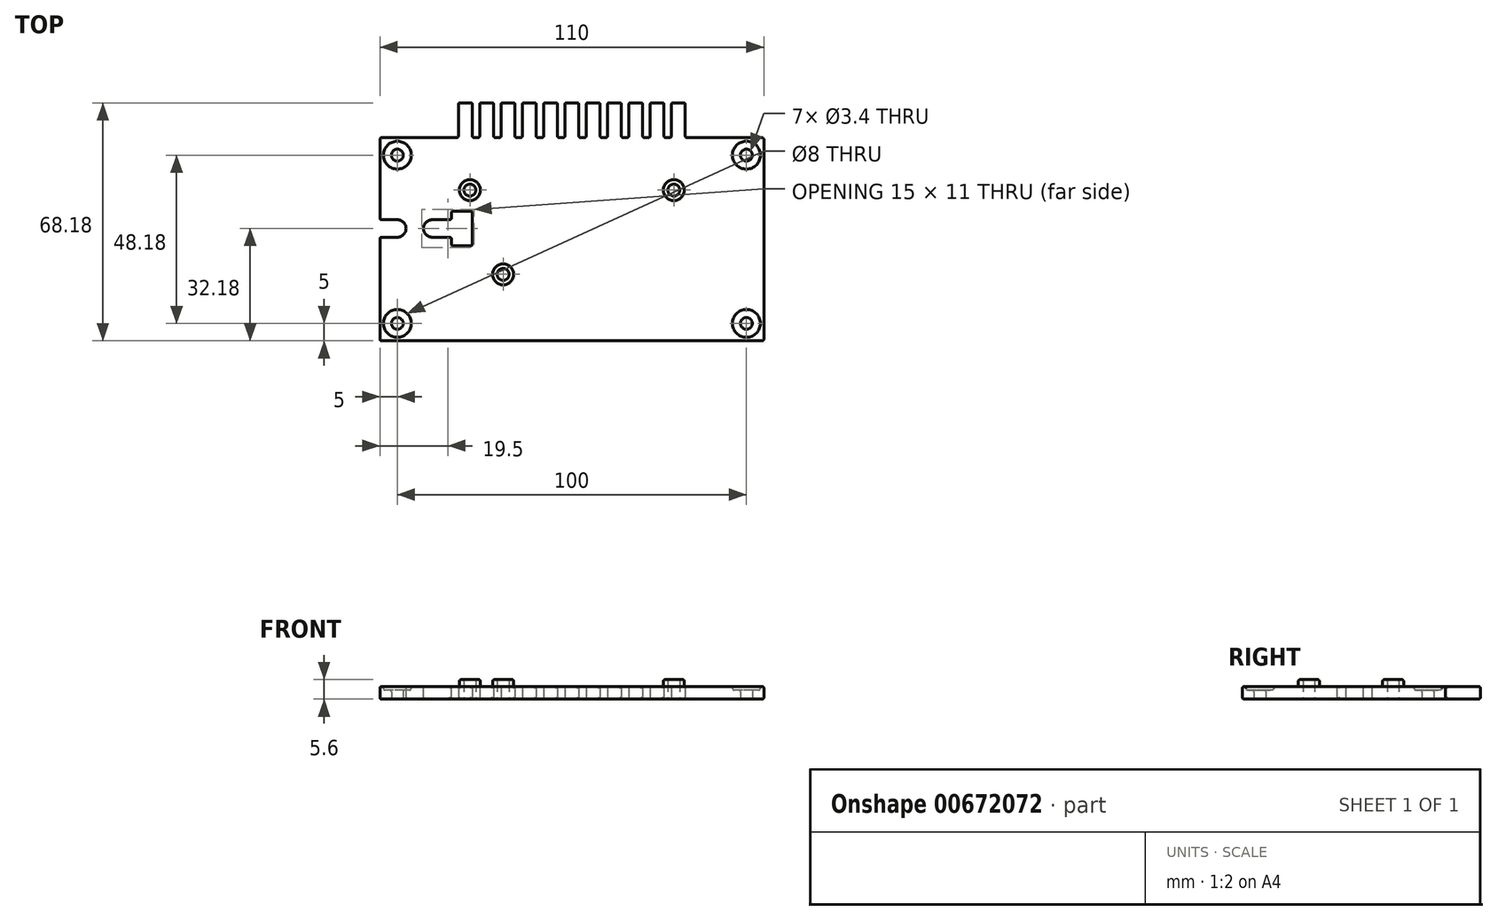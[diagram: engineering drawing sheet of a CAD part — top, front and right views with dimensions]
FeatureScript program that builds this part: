
annotation { "Feature Type Name" : "Feature", "Feature Type Description" : "" }
export const myFeature = defineFeature(function(context is Context, id is Id, definition is map)
    precondition{}
    {
        {
            var Q0;
            Q0=qCreatedBy(makeId("Top.planeOp"),FACE);
            var sketch = newSketch(context, id + "F0", { "sketchPlane" : qUnion([Q0])});
            skLineSegment(sketch, "E0.bottom", {"start": v(31.75, 16.63) * mm, "end": v(-31.75, 16.63) * mm, "construction": true});
            skLineSegment(sketch, "E0.top", {"start": v(31.75, -29.09) * mm, "end": v(-31.75, -29.09) * mm});
            skLineSegment(sketch, "E0.left", {"start": v(31.75, 16.63) * mm, "end": v(31.75, -29.1) * mm, "construction": true});
            skLineSegment(sketch, "E0.right", {"start": v(-31.75, 16.63) * mm, "end": v(-31.75, -29.1) * mm, "construction": true});
            skCircle(sketch, "E1", {"center": v(-29.21, 14.1) * mm, "radius": 1.7 * mm});
            skCircle(sketch, "E2", {"center": v(29.21, 14.1) * mm, "radius": 1.7 * mm});
            skCircle(sketch, "E3", {"center": v(-19.68, -10.04) * mm, "radius": 1.7 * mm});
            skLineSegment(sketch, "E4.bottom", {"start": v(55, 29.09) * mm, "end": v(-55, 29.09) * mm});
            skLineSegment(sketch, "E4.top", {"start": v(55, -29.09) * mm, "end": v(-55, -29.09) * mm});
            skLineSegment(sketch, "E4.left", {"start": v(55, 29.09) * mm, "end": v(55, -29.09) * mm});
            skLineSegment(sketch, "E4.right", {"start": v(-55, 29.09) * mm, "end": v(-55, -29.1) * mm});
            skPoint(sketch, "E4.middle", {"position": v(0, 0) * mm});
            skLineSegment(sketch, "E5.top", {"start": v(55, 19.09) * mm, "end": v(-55, 19.09) * mm, "construction": true});
            skLineSegment(sketch, "E5.left", {"start": v(55, 29.09) * mm, "end": v(55, 19.1) * mm});
            skLineSegment(sketch, "E5.right", {"start": v(-55, 29.09) * mm, "end": v(-55, 19.1) * mm});
            skPoint(sketch, "E5.middle", {"position": v(0, 24.09) * mm});
            skLineSegment(sketch, "E6.top", {"start": v(55, -19.1) * mm, "end": v(-55, -19.1) * mm, "construction": true});
            skLineSegment(sketch, "E6.left", {"start": v(55, -29.09) * mm, "end": v(55, -19.1) * mm});
            skLineSegment(sketch, "E6.right", {"start": v(-55, -29.09) * mm, "end": v(-55, -19.09) * mm});
            skPoint(sketch, "E6.middle", {"position": v(0, -24.09) * mm});
            skLineSegment(sketch, "E7", {"start": v(0, 16.63) * mm, "end": v(0, -29.09) * mm, "construction": true});
            skPoint(sketch, "E8", {"position": v(0, 19.09) * mm});
            skCircle(sketch, "E9", {"center": v(-50, 24.09) * mm, "radius": 1.7 * mm});
            skCircle(sketch, "E10", {"center": v(50, 24.09) * mm, "radius": 1.7 * mm});
            skCircle(sketch, "E11", {"center": v(-50, -24.09) * mm, "radius": 1.7 * mm});
            skCircle(sketch, "E12", {"center": v(50, -24.09) * mm, "radius": 1.7 * mm});
            skLineSegment(sketch, "E13.bottom", {"start": v(50, 24.09) * mm, "end": v(-50, 24.09) * mm, "construction": true});
            skLineSegment(sketch, "E13.top", {"start": v(50, -24.09) * mm, "end": v(-50, -24.09) * mm, "construction": true});
            skLineSegment(sketch, "E13.left", {"start": v(50, 24.09) * mm, "end": v(50, -24.09) * mm, "construction": true});
            skLineSegment(sketch, "E13.right", {"start": v(-50, 24.09) * mm, "end": v(-50, -24.09) * mm, "construction": true});
            skLineSegment(sketch, "E14.bottom", {"start": v(32.5, 29.09) * mm, "end": v(-32.5, 29.09) * mm});
            skLineSegment(sketch, "E14.top", {"start": v(32.5, 39.09) * mm, "end": v(-32.5, 39.09) * mm});
            skLineSegment(sketch, "E14.left", {"start": v(32.5, 29.09) * mm, "end": v(32.5, 39.09) * mm});
            skLineSegment(sketch, "E14.right", {"start": v(-32.5, 29.09) * mm, "end": v(-32.5, 39.09) * mm});
            skPoint(sketch, "E14.middle", {"position": v(0, 34.09) * mm});
            skLineSegment(sketch, "E15.bottom", {"start": v(-26.4, 39.09) * mm, "end": v(-28.5, 39.09) * mm});
            skLineSegment(sketch, "E15.top", {"start": v(-26.4, 29.09) * mm, "end": v(-28.5, 29.09) * mm});
            skLineSegment(sketch, "E15.left", {"start": v(-26.4, 39.09) * mm, "end": v(-26.4, 29.09) * mm});
            skLineSegment(sketch, "E15.right", {"start": v(-28.5, 39.09) * mm, "end": v(-28.5, 29.09) * mm});
            skPoint(sketch, "E15.middle", {"position": v(-27.45, 34.09) * mm});
            skLineSegment(sketch, "E16.1.0.0", {"start": v(-20.3, 39.09) * mm, "end": v(-20.3, 29.09) * mm});
            skLineSegment(sketch, "E16.1.0.1", {"start": v(-20.3, 39.09) * mm, "end": v(-22.4, 39.09) * mm});
            skLineSegment(sketch, "E16.1.0.2", {"start": v(-22.4, 39.09) * mm, "end": v(-22.4, 29.09) * mm});
            skLineSegment(sketch, "E16.1.0.3", {"start": v(-20.3, 29.09) * mm, "end": v(-22.4, 29.09) * mm});
            skLineSegment(sketch, "E16.2.0.0", {"start": v(-14.2, 39.09) * mm, "end": v(-14.2, 29.09) * mm});
            skLineSegment(sketch, "E16.2.0.1", {"start": v(-14.2, 39.09) * mm, "end": v(-16.3, 39.09) * mm});
            skLineSegment(sketch, "E16.2.0.2", {"start": v(-16.3, 39.09) * mm, "end": v(-16.3, 29.09) * mm});
            skLineSegment(sketch, "E16.2.0.3", {"start": v(-14.2, 29.1) * mm, "end": v(-16.3, 29.1) * mm});
            skLineSegment(sketch, "E16.3.0.0", {"start": v(-8.1, 39.09) * mm, "end": v(-8.1, 29.09) * mm});
            skLineSegment(sketch, "E16.3.0.1", {"start": v(-8.1, 39.09) * mm, "end": v(-10.2, 39.09) * mm});
            skLineSegment(sketch, "E16.3.0.2", {"start": v(-10.2, 39.09) * mm, "end": v(-10.2, 29.09) * mm});
            skLineSegment(sketch, "E16.3.0.3", {"start": v(-8.1, 29.1) * mm, "end": v(-10.2, 29.1) * mm});
            skLineSegment(sketch, "E16.4.0.0", {"start": v(-2, 39.09) * mm, "end": v(-2, 29.09) * mm});
            skLineSegment(sketch, "E16.4.0.1", {"start": v(-2, 39.09) * mm, "end": v(-4.1, 39.09) * mm});
            skLineSegment(sketch, "E16.4.0.2", {"start": v(-4.1, 39.09) * mm, "end": v(-4.1, 29.09) * mm});
            skLineSegment(sketch, "E16.4.0.3", {"start": v(-2, 29.1) * mm, "end": v(-4.1, 29.1) * mm});
            skLineSegment(sketch, "E16.5.0.0", {"start": v(4.1, 39.09) * mm, "end": v(4.1, 29.09) * mm});
            skLineSegment(sketch, "E16.5.0.1", {"start": v(4.1, 39.09) * mm, "end": v(2, 39.09) * mm});
            skLineSegment(sketch, "E16.5.0.2", {"start": v(2, 39.09) * mm, "end": v(2, 29.09) * mm});
            skLineSegment(sketch, "E16.5.0.3", {"start": v(4.1, 29.1) * mm, "end": v(2, 29.1) * mm});
            skLineSegment(sketch, "E16.6.0.0", {"start": v(10.2, 39.09) * mm, "end": v(10.2, 29.09) * mm});
            skLineSegment(sketch, "E16.6.0.1", {"start": v(10.2, 39.09) * mm, "end": v(8.1, 39.09) * mm});
            skLineSegment(sketch, "E16.6.0.2", {"start": v(8.1, 39.09) * mm, "end": v(8.1, 29.09) * mm});
            skLineSegment(sketch, "E16.6.0.3", {"start": v(10.2, 29.1) * mm, "end": v(8.1, 29.1) * mm});
            skLineSegment(sketch, "E16.direction1", {"start": v(-26.4, 29.09) * mm, "end": v(-20.3, 29.09) * mm, "construction": true});
            skLineSegment(sketch, "E17.0.7.0", {"start": v(16.3, 39.09) * mm, "end": v(16.3, 29.09) * mm});
            skLineSegment(sketch, "E17.3.7.0", {"start": v(16.3, 39.09) * mm, "end": v(14.2, 39.09) * mm});
            skLineSegment(sketch, "E17.6.7.0", {"start": v(14.2, 39.09) * mm, "end": v(14.2, 29.09) * mm});
            skLineSegment(sketch, "E17.9.7.0", {"start": v(16.3, 29.09) * mm, "end": v(14.2, 29.09) * mm});
            skLineSegment(sketch, "E17.0.8.0", {"start": v(22.4, 39.09) * mm, "end": v(22.4, 29.09) * mm});
            skLineSegment(sketch, "E17.3.8.0", {"start": v(22.4, 39.09) * mm, "end": v(20.3, 39.09) * mm});
            skLineSegment(sketch, "E17.6.8.0", {"start": v(20.3, 39.09) * mm, "end": v(20.3, 29.09) * mm});
            skLineSegment(sketch, "E17.9.8.0", {"start": v(22.4, 29.09) * mm, "end": v(20.3, 29.09) * mm});
            skLineSegment(sketch, "E17.0.9.0", {"start": v(28.5, 39.09) * mm, "end": v(28.5, 29.09) * mm});
            skLineSegment(sketch, "E17.3.9.0", {"start": v(28.5, 39.09) * mm, "end": v(26.4, 39.09) * mm});
            skLineSegment(sketch, "E17.6.9.0", {"start": v(26.4, 39.09) * mm, "end": v(26.4, 29.09) * mm});
            skLineSegment(sketch, "E17.9.9.0", {"start": v(28.5, 29.09) * mm, "end": v(26.4, 29.09) * mm});
            skLineSegment(sketch, "E18", {"start": v(-2, 34.09) * mm, "end": v(2, 34.09) * mm, "construction": true});
            skSolve(sketch);
        }
        {
            var Q0;
            Q0=makeQuery(id+"F0.imprint","IMPRINT",FACE,{"disambiguationData":[TD([[makeQuery(id+"F0.imprint","IMPRINT",EDGE,{"derivedFrom":sQuery(id+"F0.wireOp",EDGE,"E1")}),-1.0]])]});
            var Q1;
            {var subQ0=sQuery(id+"F0.wireOp",EDGE,"E14.right");Q1=makeQuery(id+"F0.imprint","IMPRINT",FACE,{"disambiguationData":[TD([[makeQuery(id+"F0.imprint","IMPRINT",EDGE,{"derivedFrom":subQ0}),-1.0]])]});}
            var Q2;
            {var subQ0=sQuery(id+"F0.wireOp",EDGE,"E15.left");Q2=makeQuery(id+"F0.imprint","IMPRINT",FACE,{"disambiguationData":[TD([[makeQuery(id+"F0.imprint","IMPRINT",EDGE,{"derivedFrom":subQ0}),1.0]])]});}
            var Q3;
            {var subQ0=sQuery(id+"F0.wireOp",EDGE,"E16.1.0.0");Q3=makeQuery(id+"F0.imprint","IMPRINT",FACE,{"disambiguationData":[TD([[makeQuery(id+"F0.imprint","IMPRINT",EDGE,{"derivedFrom":subQ0}),1.0]])]});}
            var Q4;
            {var subQ0=sQuery(id+"F0.wireOp",EDGE,"E16.2.0.0");Q4=makeQuery(id+"F0.imprint","IMPRINT",FACE,{"disambiguationData":[TD([[makeQuery(id+"F0.imprint","IMPRINT",EDGE,{"derivedFrom":subQ0}),1.0]])]});}
            var Q5;
            {var subQ0=sQuery(id+"F0.wireOp",EDGE,"E16.3.0.0");Q5=makeQuery(id+"F0.imprint","IMPRINT",FACE,{"disambiguationData":[TD([[makeQuery(id+"F0.imprint","IMPRINT",EDGE,{"derivedFrom":subQ0}),1.0]])]});}
            var Q6;
            {var subQ0=sQuery(id+"F0.wireOp",EDGE,"E16.4.0.0");Q6=makeQuery(id+"F0.imprint","IMPRINT",FACE,{"disambiguationData":[TD([[makeQuery(id+"F0.imprint","IMPRINT",EDGE,{"derivedFrom":subQ0}),1.0]])]});}
            var Q7;
            {var subQ0=sQuery(id+"F0.wireOp",EDGE,"E16.5.0.0");Q7=makeQuery(id+"F0.imprint","IMPRINT",FACE,{"disambiguationData":[TD([[makeQuery(id+"F0.imprint","IMPRINT",EDGE,{"derivedFrom":subQ0}),1.0]])]});}
            var Q8;
            {var subQ0=sQuery(id+"F0.wireOp",EDGE,"E16.6.0.0");Q8=makeQuery(id+"F0.imprint","IMPRINT",FACE,{"disambiguationData":[TD([[makeQuery(id+"F0.imprint","IMPRINT",EDGE,{"derivedFrom":subQ0}),1.0]])]});}
            var Q9;
            {var subQ0=sQuery(id+"F0.wireOp",EDGE,"E17.0.7.0");Q9=makeQuery(id+"F0.imprint","IMPRINT",FACE,{"disambiguationData":[TD([[makeQuery(id+"F0.imprint","IMPRINT",EDGE,{"derivedFrom":subQ0}),1.0]])]});}
            var Q10;
            {var subQ0=sQuery(id+"F0.wireOp",EDGE,"E17.0.8.0");Q10=makeQuery(id+"F0.imprint","IMPRINT",FACE,{"disambiguationData":[TD([[makeQuery(id+"F0.imprint","IMPRINT",EDGE,{"derivedFrom":subQ0}),1.0]])]});}
            var Q11;
            {var subQ0=sQuery(id+"F0.wireOp",EDGE,"E14.left");Q11=makeQuery(id+"F0.imprint","IMPRINT",FACE,{"disambiguationData":[TD([[makeQuery(id+"F0.imprint","IMPRINT",EDGE,{"derivedFrom":subQ0}),1.0]])]});}
            extrude(context, id + "F1", {"entities" : qUnion([Q0, Q1, Q2, Q3, Q4, Q5, Q6, Q7, Q8, Q9, Q10, Q11]), "depth" : 3.6 * mm, "offsetDistance" : 25 * mm});
        }
        {
            var Q0;
            Q0=makeQuery(id+"F1.opExtrude","CAP_FACE",FACE,{"disambiguationData":[OSD([sQuery(id+"F0.wireOp",EDGE,"E1"),sQuery(id+"F0.wireOp",EDGE,"E2"),sQuery(id+"F0.wireOp",EDGE,"E3"),sQuery(id+"F0.wireOp",EDGE,"E4.left"),sQuery(id+"F0.wireOp",EDGE,"E4.right"),sQuery(id+"F0.wireOp",EDGE,"E4.bottom"),sQuery(id+"F0.wireOp",EDGE,"E5.left"),sQuery(id+"F0.wireOp",EDGE,"E5.right"),sQuery(id+"F0.wireOp",EDGE,"E4.top"),sQuery(id+"F0.wireOp",EDGE,"E6.left"),sQuery(id+"F0.wireOp",EDGE,"E6.right"),sQuery(id+"F0.wireOp",EDGE,"E9"),sQuery(id+"F0.wireOp",EDGE,"E10"),sQuery(id+"F0.wireOp",EDGE,"E11"),sQuery(id+"F0.wireOp",EDGE,"E12")])],"isStart":false});
            var sketch = newSketch(context, id + "F2", { "sketchPlane" : qUnion([Q0])});
            skCircle(sketch, "E19", {"center": v(-50, 24.09) * mm, "radius": 4 * mm});
            skCircle(sketch, "E20", {"center": v(50, 24.09) * mm, "radius": 4 * mm});
            skCircle(sketch, "E21", {"center": v(-50, -24.09) * mm, "radius": 4 * mm});
            skCircle(sketch, "E22", {"center": v(50, -24.09) * mm, "radius": 4 * mm});
            skCircle(sketch, "E23", {"center": v(-29.21, 14.1) * mm, "radius": 3 * mm});
            skCircle(sketch, "E24", {"center": v(-19.68, -10.04) * mm, "radius": 3 * mm});
            skCircle(sketch, "E25", {"center": v(29.21, 14.1) * mm, "radius": 3 * mm});
            skCircle(sketch, "E26", {"center": v(-50, 3.09) * mm, "radius": 2.5 * mm});
            skCircle(sketch, "E27", {"center": v(-40, 3.09) * mm, "radius": 2.5 * mm});
            skLineSegment(sketch, "E28", {"start": v(-50, 3.1) * mm, "end": v(-55, 3.1) * mm, "construction": true});
            skLineSegment(sketch, "E29", {"start": v(-40, 3.1) * mm, "end": v(-31.75, 3.1) * mm, "construction": true});
            skLineSegment(sketch, "E30.bottom", {"start": v(-34.5, -1.91) * mm, "end": v(-28.5, -1.91) * mm});
            skLineSegment(sketch, "E30.top", {"start": v(-34.5, 8.1) * mm, "end": v(-28.5, 8.1) * mm});
            skLineSegment(sketch, "E30.left", {"start": v(-34.5, -1.9) * mm, "end": v(-34.5, 8.09) * mm});
            skLineSegment(sketch, "E30.right", {"start": v(-28.5, -1.9) * mm, "end": v(-28.5, 8.1) * mm});
            skPoint(sketch, "E31", {"position": v(-34.5, 3.09) * mm});
            skLineSegment(sketch, "E32", {"start": v(-40, 5.59) * mm, "end": v(-34.5, 5.59) * mm});
            skLineSegment(sketch, "E33", {"start": v(-40, 0.59) * mm, "end": v(-34.5, 0.59) * mm});
            skLineSegment(sketch, "E34", {"start": v(-55, 0.59) * mm, "end": v(-50, 0.59) * mm});
            skLineSegment(sketch, "E35", {"start": v(-50, 5.59) * mm, "end": v(-55, 5.59) * mm});
            skSolve(sketch);
        }
        {
            var Q0;
            Q0=makeQuery(id+"F2.imprint","IMPRINT",FACE,{"disambiguationData":[TD([[makeQuery(id+"F2.imprint","IMPRINT",EDGE,{"derivedFrom":sQuery(id+"F2.wireOp",EDGE,"E19")}),1.0]])]});
            var Q1;
            Q1=makeQuery(id+"F2.imprint","IMPRINT",FACE,{"disambiguationData":[TD([[makeQuery(id+"F2.imprint","IMPRINT",EDGE,{"derivedFrom":sQuery(id+"F2.wireOp",EDGE,"E20")}),1.0]])]});
            var Q2;
            Q2=makeQuery(id+"F2.imprint","IMPRINT",FACE,{"disambiguationData":[TD([[makeQuery(id+"F2.imprint","IMPRINT",EDGE,{"derivedFrom":sQuery(id+"F2.wireOp",EDGE,"E22")}),1.0]])]});
            var Q3;
            Q3=makeQuery(id+"F2.imprint","IMPRINT",FACE,{"disambiguationData":[TD([[makeQuery(id+"F2.imprint","IMPRINT",EDGE,{"derivedFrom":sQuery(id+"F2.wireOp",EDGE,"E21")}),1.0]])]});
            extrude(context, id + "F3", {"entities" : qUnion([Q0, Q1, Q2, Q3]), "operationType" : NewBodyOperationType.REMOVE, "oppositeDirection" : true, "depth" : (3.6 - 2.6) * mm, "offsetDistance" : 25 * mm});
        }
        {
            var Q0;
            Q0=makeQuery(id+"F2.imprint","IMPRINT",FACE,{"disambiguationData":[TD([[makeQuery(id+"F2.imprint","IMPRINT",EDGE,{"derivedFrom":sQuery(id+"F2.wireOp",EDGE,"E23")}),1.0]])]});
            var Q1;
            Q1=makeQuery(id+"F2.imprint","IMPRINT",FACE,{"disambiguationData":[TD([[makeQuery(id+"F2.imprint","IMPRINT",EDGE,{"derivedFrom":sQuery(id+"F2.wireOp",EDGE,"E24")}),1.0]])]});
            var Q2;
            Q2=makeQuery(id+"F2.imprint","IMPRINT",FACE,{"disambiguationData":[TD([[makeQuery(id+"F2.imprint","IMPRINT",EDGE,{"derivedFrom":sQuery(id+"F2.wireOp",EDGE,"E25")}),1.0]])]});
            extrude(context, id + "F4", {"entities" : qUnion([Q0, Q1, Q2]), "operationType" : NewBodyOperationType.ADD, "depth" : 2 * mm, "offsetDistance" : 25 * mm});
        }
        {
            var Q0;
            {var subQ3=sQuery(id+"F2.wireOp",EDGE,"E30.bottom");Q0=makeQuery(id+"F2.imprint","IMPRINT",FACE,{"disambiguationData":[TD([[makeQuery(id+"F2.imprint","IMPRINT",EDGE,{"derivedFrom":subQ3}),1.0]])]});}
            var Q1;
            {var subQ0=sQuery(id+"F2.wireOp",EDGE,"E32");Q1=makeQuery(id+"F2.imprint","IMPRINT",FACE,{"disambiguationData":[TD([[makeQuery(id+"F2.imprint","IMPRINT",EDGE,{"derivedFrom":subQ0}),-1.0]])]});}
            var Q2;
            {var subQ0=sQuery(id+"F2.wireOp",EDGE,"E27");var subQ1=makeQuery(id+"F2.imprint","INTERSECT",VERTEX,{"derivedFrom":[subQ0,sQuery(id+"F2.wireOp",EDGE,"E32")]});Q2=makeQuery(id+"F2.imprint","IMPRINT",FACE,{"disambiguationData":[TD([[makeQuery(id+"F2.imprint","IMPRINT",EDGE,{"disambiguationData":[TD([[subQ1,-1.0]])],"derivedFrom":subQ0}),1.0]])]});}
            var Q3;
            Q3=makeQuery(id+"F2.imprint","IMPRINT",FACE,{"disambiguationData":[TD([[makeQuery(id+"F2.imprint","IMPRINT",EDGE,{"derivedFrom":sQuery(id+"F2.wireOp",EDGE,"E26")}),1.0]])]});
            var Q4;
            Q4=makeQuery(id+"F2.imprint","IMPRINT",FACE,{"disambiguationData":[TD([[makeQuery(id+"F2.imprint","IMPRINT",EDGE,{"derivedFrom":sQuery(id+"F2.wireOp",EDGE,"tUUgJWzo-lUW7-Ycnc-b3Et-vA79GdTYksxT")}),1.0]])]});
            var Q5;
            Q5=makeQuery(id+"F2.imprint","IMPRINT",FACE,{"disambiguationData":[TD([[makeQuery(id+"F2.imprint","IMPRINT",EDGE,{"derivedFrom":sQuery(id+"F2.wireOp",EDGE,"KURrdWEJ-psNY-TnCP-ahzj-soCBxva00qhG")}),1.0]])]});
            var Q6;
            {var subQ0=sQuery(id+"F2.wireOp",EDGE,"E34");Q6=makeQuery(id+"F2.imprint","IMPRINT",FACE,{"disambiguationData":[TD([[makeQuery(id+"F2.imprint","IMPRINT",EDGE,{"derivedFrom":subQ0}),1.0]])]});}
            extrude(context, id + "F5", {"entities" : qUnion([Q0, Q1, Q2, Q3, Q4, Q5, Q6]), "operationType" : NewBodyOperationType.REMOVE, "oppositeDirection" : true, "depth" : 25 * mm, "offsetDistance" : 25 * mm});
        }
        {
            var Q0;
            Q0=makeQuery(id+"F1.opExtrude","CAP_EDGE",EDGE,{"disambiguationData":[OSD([sQuery(id+"F0.wireOp",EDGE,"E4.bottom")])],"isStart":false});
            var Q1;
            Q1=makeQuery(id+"F1.opExtrude","SWEPT_FACE",FACE,{"disambiguationData":[OSD([sQuery(id+"F0.wireOp",EDGE,"E9")])]});
            var Q2;
            Q2=makeQuery(id+"F1.opExtrude","SWEPT_FACE",FACE,{"disambiguationData":[OSD([sQuery(id+"F0.wireOp",EDGE,"E1")])]});
            var Q3;
            Q3=makeQuery(id+"F1.opExtrude","SWEPT_FACE",FACE,{"disambiguationData":[OSD([sQuery(id+"F0.wireOp",EDGE,"E3")])]});
            var Q4;
            Q4=makeQuery(id+"F1.opExtrude","SWEPT_FACE",FACE,{"disambiguationData":[OSD([sQuery(id+"F0.wireOp",EDGE,"E11")])]});
            var Q5;
            Q5=makeQuery(id+"F1.opExtrude","SWEPT_FACE",FACE,{"disambiguationData":[OSD([sQuery(id+"F0.wireOp",EDGE,"E2")])]});
            var Q6;
            Q6=makeQuery(id+"F1.opExtrude","SWEPT_FACE",FACE,{"disambiguationData":[OSD([sQuery(id+"F0.wireOp",EDGE,"E10")])]});
            var Q7;
            Q7=makeQuery(id+"F1.opExtrude","SWEPT_FACE",FACE,{"disambiguationData":[OSD([sQuery(id+"F0.wireOp",EDGE,"E12")])]});
            var Q8;
            Q8=makeQuery(id+"F1.opExtrude","SWEPT_FACE",FACE,{"disambiguationData":[OSD([sQuery(id+"F0.wireOp",EDGE,"E4.left"),sQuery(id+"F0.wireOp",EDGE,"E5.left"),sQuery(id+"F0.wireOp",EDGE,"E6.left")])]});
            var Q9;
            Q9=makeQuery(id+"F1.opExtrude","SWEPT_FACE",FACE,{"disambiguationData":[OSD([sQuery(id+"F0.wireOp",EDGE,"E4.top")])]});
            var Q10;
            Q10=makeQuery(id+"F1.opExtrude","SWEPT_FACE",FACE,{"disambiguationData":[OSD([sQuery(id+"F0.wireOp",EDGE,"E4.right"),sQuery(id+"F0.wireOp",EDGE,"E5.right"),sQuery(id+"F0.wireOp",EDGE,"E6.right")])]});
            var Q11;
            Q11=makeQuery(id+"F1.opExtrude","CAP_EDGE",EDGE,{"disambiguationData":[OSD([sQuery(id+"F0.wireOp",EDGE,"E4.bottom")])],"isStart":true});
            var Q12;
            {var subQ0=sQuery(id+"F2.wireOp",EDGE,"E30.left");Q12=makeQuery(id+"F5.boolean.opBoolean","COPY",FACE,{"derivedFrom":makeQuery(id+"F5.opExtrude","SWEPT_FACE",FACE,{"disambiguationData":[OSD([subQ0]),TDD([makeQuery(id+"F2.imprint","IMPRINT",EDGE,{"disambiguationData":[TD([[makeQuery(id+"F2.imprint","INTERSECT",VERTEX,{"derivedFrom":[sQuery(id+"F2.wireOp",EDGE,"E30.top"),subQ0]}),1.0]])],"derivedFrom":subQ0})])]})});}
            var Q13;
            Q13=makeQuery(id+"F5.boolean.opBoolean","COPY",FACE,{"derivedFrom":makeQuery(id+"F5.opExtrude","SWEPT_FACE",FACE,{"disambiguationData":[OSD([sQuery(id+"F2.wireOp",EDGE,"E30.top")])]})});
            var Q14;
            Q14=makeQuery(id+"F5.boolean.opBoolean","COPY",FACE,{"derivedFrom":makeQuery(id+"F5.opExtrude","SWEPT_FACE",FACE,{"disambiguationData":[OSD([sQuery(id+"F2.wireOp",EDGE,"E30.right")])]})});
            var Q15;
            Q15=makeQuery(id+"F5.boolean.opBoolean","COPY",FACE,{"derivedFrom":makeQuery(id+"F5.opExtrude","SWEPT_FACE",FACE,{"disambiguationData":[OSD([sQuery(id+"F2.wireOp",EDGE,"E30.bottom")])]})});
            var Q16;
            Q16=makeQuery(id+"F5.boolean.opBoolean","COPY",FACE,{"derivedFrom":makeQuery(id+"F5.opExtrude","SWEPT_FACE",FACE,{"disambiguationData":[OSD([sQuery(id+"F2.wireOp",EDGE,"E33")])]})});
            var Q17;
            Q17=makeQuery(id+"F5.boolean.opBoolean","COPY",FACE,{"derivedFrom":makeQuery(id+"F5.opExtrude","SWEPT_FACE",FACE,{"disambiguationData":[OSD([sQuery(id+"F2.wireOp",EDGE,"E27")])]})});
            var Q18;
            Q18=makeQuery(id+"F5.boolean.opBoolean","COPY",FACE,{"derivedFrom":makeQuery(id+"F5.opExtrude","SWEPT_FACE",FACE,{"disambiguationData":[OSD([sQuery(id+"F2.wireOp",EDGE,"E26")])]})});
            var Q19;
            Q19=makeQuery(id+"F5.boolean.opBoolean","COPY",FACE,{"derivedFrom":makeQuery(id+"F5.opExtrude","SWEPT_FACE",FACE,{"disambiguationData":[OSD([sQuery(id+"F2.wireOp",EDGE,"E32")])]})});
            var Q20;
            Q20=makeQuery(id+"F4.opExtrude","CAP_EDGE",EDGE,{"disambiguationData":[OSD([sQuery(id+"F2.wireOp",EDGE,"E24")])],"isStart":false});
            var Q21;
            Q21=makeQuery(id+"F4.opExtrude","CAP_EDGE",EDGE,{"disambiguationData":[OSD([sQuery(id+"F2.wireOp",EDGE,"E24")])],"isStart":true});
            var Q22;
            Q22=makeQuery(id+"F4.opExtrude","CAP_EDGE",EDGE,{"disambiguationData":[OSD([sQuery(id+"F2.wireOp",EDGE,"E23")])],"isStart":true});
            var Q23;
            Q23=makeQuery(id+"F4.opExtrude","CAP_EDGE",EDGE,{"disambiguationData":[OSD([sQuery(id+"F2.wireOp",EDGE,"E23")])],"isStart":false});
            var Q24;
            Q24=makeQuery(id+"F4.opExtrude","CAP_EDGE",EDGE,{"disambiguationData":[OSD([sQuery(id+"F2.wireOp",EDGE,"E25")])],"isStart":false});
            var Q25;
            Q25=makeQuery(id+"F4.opExtrude","SWEPT_FACE",FACE,{"disambiguationData":[OSD([sQuery(id+"F2.wireOp",EDGE,"E25")])]});
            var Q26;
            Q26=makeQuery(id+"F3.boolean.opBoolean","COPY",FACE,{"derivedFrom":makeQuery(id+"F3.opExtrude","SWEPT_FACE",FACE,{"disambiguationData":[OSD([sQuery(id+"F2.wireOp",EDGE,"E22")])]})});
            var Q27;
            Q27=makeQuery(id+"F3.boolean.opBoolean","COPY",EDGE,{"derivedFrom":makeQuery(id+"F3.opExtrude","CAP_EDGE",EDGE,{"disambiguationData":[OSD([sQuery(id+"F2.wireOp",EDGE,"E21")])],"isStart":false})});
            var Q28;
            Q28=makeQuery(id+"F3.boolean.opBoolean","COPY",EDGE,{"derivedFrom":makeQuery(id+"F3.opExtrude","CAP_EDGE",EDGE,{"disambiguationData":[OSD([sQuery(id+"F2.wireOp",EDGE,"E21")])],"isStart":true})});
            var Q29;
            Q29=makeQuery(id+"F3.boolean.opBoolean","COPY",FACE,{"derivedFrom":makeQuery(id+"F3.opExtrude","SWEPT_FACE",FACE,{"disambiguationData":[OSD([sQuery(id+"F2.wireOp",EDGE,"E19")])]})});
            var Q30;
            Q30=makeQuery(id+"F3.boolean.opBoolean","COPY",FACE,{"derivedFrom":makeQuery(id+"F3.opExtrude","SWEPT_FACE",FACE,{"disambiguationData":[OSD([sQuery(id+"F2.wireOp",EDGE,"E20")])]})});
            var Q31;
            Q31=makeQuery(id+"F5.boolean.opBoolean","COPY",FACE,{"derivedFrom":makeQuery(id+"F5.opExtrude","SWEPT_FACE",FACE,{"disambiguationData":[OSD([sQuery(id+"F2.wireOp",EDGE,"tUUgJWzo-lUW7-Ycnc-b3Et-vA79GdTYksxT")])]})});
            var Q32;
            Q32=makeQuery(id+"F5.boolean.opBoolean","COPY",FACE,{"derivedFrom":makeQuery(id+"F5.opExtrude","SWEPT_FACE",FACE,{"disambiguationData":[OSD([sQuery(id+"F2.wireOp",EDGE,"KURrdWEJ-psNY-TnCP-ahzj-soCBxva00qhG")])]})});
            var Q33;
            Q33=makeQuery(id+"F5.boolean.opBoolean","COPY",FACE,{"derivedFrom":makeQuery(id+"F5.opExtrude","SWEPT_FACE",FACE,{"disambiguationData":[OSD([sQuery(id+"F2.wireOp",EDGE,"E35")])]})});
            var Q34;
            Q34=makeQuery(id+"F5.boolean.opBoolean","COPY",FACE,{"derivedFrom":makeQuery(id+"F5.opExtrude","SWEPT_FACE",FACE,{"disambiguationData":[OSD([sQuery(id+"F2.wireOp",EDGE,"E34")])]})});
            var Q35;
            {var subQ0=sQuery(id+"F0.wireOp",EDGE,"E14.top");Q35=makeQuery(id+"F1.opExtrude","SWEPT_FACE",FACE,{"disambiguationData":[OSD([subQ0]),TDD([makeQuery(id+"F0.imprint","IMPRINT",EDGE,{"disambiguationData":[TD([[makeQuery(id+"F0.imprint","INTERSECT",VERTEX,{"derivedFrom":[subQ0,sQuery(id+"F0.wireOp",EDGE,"E14.left")]}),-1.0]])],"derivedFrom":subQ0})])]});}
            var Q36;
            {var subQ0=sQuery(id+"F0.wireOp",EDGE,"E14.top");Q36=makeQuery(id+"F1.opExtrude","SWEPT_FACE",FACE,{"disambiguationData":[OSD([subQ0]),TDD([makeQuery(id+"F0.imprint","IMPRINT",EDGE,{"disambiguationData":[TD([[makeQuery(id+"F0.imprint","INTERSECT",VERTEX,{"derivedFrom":[subQ0,sQuery(id+"F0.wireOp",EDGE,"E17.0.8.0"),sQuery(id+"F0.wireOp",EDGE,"E17.3.8.0")]}),1.0]])],"derivedFrom":subQ0})])]});}
            var Q37;
            {var subQ0=sQuery(id+"F0.wireOp",EDGE,"E14.top");Q37=makeQuery(id+"F1.opExtrude","SWEPT_FACE",FACE,{"disambiguationData":[OSD([subQ0]),TDD([makeQuery(id+"F0.imprint","IMPRINT",EDGE,{"disambiguationData":[TD([[makeQuery(id+"F0.imprint","INTERSECT",VERTEX,{"derivedFrom":[subQ0,sQuery(id+"F0.wireOp",EDGE,"E17.0.7.0"),sQuery(id+"F0.wireOp",EDGE,"E17.3.7.0")]}),1.0]])],"derivedFrom":subQ0})])]});}
            var Q38;
            {var subQ0=sQuery(id+"F0.wireOp",EDGE,"E14.top");Q38=makeQuery(id+"F1.opExtrude","SWEPT_FACE",FACE,{"disambiguationData":[OSD([subQ0]),TDD([makeQuery(id+"F0.imprint","IMPRINT",EDGE,{"disambiguationData":[TD([[makeQuery(id+"F0.imprint","INTERSECT",VERTEX,{"derivedFrom":[subQ0,sQuery(id+"F0.wireOp",EDGE,"E16.6.0.0"),sQuery(id+"F0.wireOp",EDGE,"E16.6.0.1")]}),1.0]])],"derivedFrom":subQ0})])]});}
            var Q39;
            {var subQ0=sQuery(id+"F0.wireOp",EDGE,"E14.top");Q39=makeQuery(id+"F1.opExtrude","SWEPT_FACE",FACE,{"disambiguationData":[OSD([subQ0]),TDD([makeQuery(id+"F0.imprint","IMPRINT",EDGE,{"disambiguationData":[TD([[makeQuery(id+"F0.imprint","INTERSECT",VERTEX,{"derivedFrom":[subQ0,sQuery(id+"F0.wireOp",EDGE,"E16.5.0.0"),sQuery(id+"F0.wireOp",EDGE,"E16.5.0.1")]}),1.0]])],"derivedFrom":subQ0})])]});}
            var Q40;
            Q40=makeQuery(id+"F1.opExtrude","SWEPT_EDGE",EDGE,{"disambiguationData":[OSD([sQuery(id+"F0.wireOp",EDGE,"E14.top"),sQuery(id+"F0.wireOp",EDGE,"E16.5.0.1"),sQuery(id+"F0.wireOp",EDGE,"E16.5.0.2")])]});
            var Q41;
            {var subQ0=sQuery(id+"F0.wireOp",EDGE,"E14.top");Q41=makeQuery(id+"F1.opExtrude","SWEPT_FACE",FACE,{"disambiguationData":[OSD([subQ0]),TDD([makeQuery(id+"F0.imprint","IMPRINT",EDGE,{"disambiguationData":[TD([[makeQuery(id+"F0.imprint","INTERSECT",VERTEX,{"derivedFrom":[subQ0,sQuery(id+"F0.wireOp",EDGE,"E16.3.0.0"),sQuery(id+"F0.wireOp",EDGE,"E16.3.0.1")]}),1.0]])],"derivedFrom":subQ0})])]});}
            var Q42;
            {var subQ0=sQuery(id+"F0.wireOp",EDGE,"E14.top");Q42=makeQuery(id+"F1.opExtrude","SWEPT_FACE",FACE,{"disambiguationData":[OSD([subQ0]),TDD([makeQuery(id+"F0.imprint","IMPRINT",EDGE,{"disambiguationData":[TD([[makeQuery(id+"F0.imprint","INTERSECT",VERTEX,{"derivedFrom":[subQ0,sQuery(id+"F0.wireOp",EDGE,"E16.2.0.0"),sQuery(id+"F0.wireOp",EDGE,"E16.2.0.1")]}),1.0]])],"derivedFrom":subQ0})])]});}
            var Q43;
            {var subQ0=sQuery(id+"F0.wireOp",EDGE,"E14.top");Q43=makeQuery(id+"F1.opExtrude","SWEPT_FACE",FACE,{"disambiguationData":[OSD([subQ0]),TDD([makeQuery(id+"F0.imprint","IMPRINT",EDGE,{"disambiguationData":[TD([[makeQuery(id+"F0.imprint","INTERSECT",VERTEX,{"derivedFrom":[subQ0,sQuery(id+"F0.wireOp",EDGE,"E16.1.0.0"),sQuery(id+"F0.wireOp",EDGE,"E16.1.0.1")]}),1.0]])],"derivedFrom":subQ0})])]});}
            var Q44;
            {var subQ0=sQuery(id+"F0.wireOp",EDGE,"E14.top");Q44=makeQuery(id+"F1.opExtrude","SWEPT_FACE",FACE,{"disambiguationData":[OSD([subQ0]),TDD([makeQuery(id+"F0.imprint","IMPRINT",EDGE,{"disambiguationData":[TD([[makeQuery(id+"F0.imprint","INTERSECT",VERTEX,{"derivedFrom":[subQ0,sQuery(id+"F0.wireOp",EDGE,"E15.bottom"),sQuery(id+"F0.wireOp",EDGE,"E15.left")]}),1.0]])],"derivedFrom":subQ0})])]});}
            var Q45;
            {var subQ0=sQuery(id+"F0.wireOp",EDGE,"E14.top");Q45=makeQuery(id+"F1.opExtrude","SWEPT_FACE",FACE,{"disambiguationData":[OSD([subQ0]),TDD([makeQuery(id+"F0.imprint","IMPRINT",EDGE,{"disambiguationData":[TD([[makeQuery(id+"F0.imprint","INTERSECT",VERTEX,{"derivedFrom":[subQ0,sQuery(id+"F0.wireOp",EDGE,"E14.right")]}),1.0]])],"derivedFrom":subQ0})])]});}
            var Q46;
            {var subQ0=sQuery(id+"F0.wireOp",EDGE,"E4.bottom");Q46=makeQuery(id+"F1.opExtrude","SWEPT_FACE",FACE,{"disambiguationData":[OSD([subQ0]),TDD([makeQuery(id+"F0.imprint","IMPRINT",EDGE,{"disambiguationData":[TD([[makeQuery(id+"F0.imprint","INTERSECT",VERTEX,{"derivedFrom":[subQ0,sQuery(id+"F0.wireOp",EDGE,"E5.right")]}),1.0]])],"derivedFrom":subQ0})])]});}
            var Q47;
            Q47=makeQuery(id+"F1.opExtrude","SWEPT_FACE",FACE,{"disambiguationData":[OSD([sQuery(id+"F0.wireOp",EDGE,"E15.top")])]});
            var Q48;
            Q48=makeQuery(id+"F1.opExtrude","SWEPT_FACE",FACE,{"disambiguationData":[OSD([sQuery(id+"F0.wireOp",EDGE,"E16.1.0.3")])]});
            var Q49;
            Q49=makeQuery(id+"F1.opExtrude","SWEPT_FACE",FACE,{"disambiguationData":[OSD([sQuery(id+"F0.wireOp",EDGE,"E17.9.9.0")])]});
            var Q50;
            Q50=makeQuery(id+"F1.opExtrude","SWEPT_FACE",FACE,{"disambiguationData":[OSD([sQuery(id+"F0.wireOp",EDGE,"E17.9.8.0")])]});
            var Q51;
            Q51=makeQuery(id+"F1.opExtrude","SWEPT_FACE",FACE,{"disambiguationData":[OSD([sQuery(id+"F0.wireOp",EDGE,"E17.9.7.0")])]});
            var Q52;
            Q52=makeQuery(id+"F1.opExtrude","SWEPT_FACE",FACE,{"disambiguationData":[OSD([sQuery(id+"F0.wireOp",EDGE,"E16.6.0.3")])]});
            var Q53;
            Q53=makeQuery(id+"F1.opExtrude","SWEPT_FACE",FACE,{"disambiguationData":[OSD([sQuery(id+"F0.wireOp",EDGE,"E16.5.0.3")])]});
            var Q54;
            Q54=makeQuery(id+"F1.opExtrude","SWEPT_FACE",FACE,{"disambiguationData":[OSD([sQuery(id+"F0.wireOp",EDGE,"E16.4.0.3")])]});
            var Q55;
            Q55=makeQuery(id+"F1.opExtrude","SWEPT_FACE",FACE,{"disambiguationData":[OSD([sQuery(id+"F0.wireOp",EDGE,"E16.3.0.3")])]});
            var Q56;
            Q56=makeQuery(id+"F1.opExtrude","SWEPT_FACE",FACE,{"disambiguationData":[OSD([sQuery(id+"F0.wireOp",EDGE,"E16.2.0.3")])]});
            var Q57;
            {var subQ0=sQuery(id+"F0.wireOp",EDGE,"E14.top");Q57=makeQuery(id+"F1.opExtrude","SWEPT_FACE",FACE,{"disambiguationData":[OSD([subQ0]),TDD([makeQuery(id+"F0.imprint","IMPRINT",EDGE,{"disambiguationData":[TD([[makeQuery(id+"F0.imprint","INTERSECT",VERTEX,{"derivedFrom":[subQ0,sQuery(id+"F0.wireOp",EDGE,"E16.4.0.0"),sQuery(id+"F0.wireOp",EDGE,"E16.4.0.1")]}),1.0]])],"derivedFrom":subQ0})])]});}
            var Q58;
            Q58=makeQuery(id+"F1.opExtrude","SWEPT_FACE",FACE,{"disambiguationData":[OSD([sQuery(id+"F0.wireOp",EDGE,"E17.0.9.0")])]});
            var Q59;
            Q59=makeQuery(id+"F1.opExtrude","SWEPT_FACE",FACE,{"disambiguationData":[OSD([sQuery(id+"F0.wireOp",EDGE,"E17.0.8.0")])]});
            var Q60;
            Q60=makeQuery(id+"F1.opExtrude","SWEPT_FACE",FACE,{"disambiguationData":[OSD([sQuery(id+"F0.wireOp",EDGE,"E17.0.7.0")])]});
            var Q61;
            Q61=makeQuery(id+"F1.opExtrude","SWEPT_FACE",FACE,{"disambiguationData":[OSD([sQuery(id+"F0.wireOp",EDGE,"E16.6.0.0")])]});
            var Q62;
            Q62=makeQuery(id+"F1.opExtrude","SWEPT_FACE",FACE,{"disambiguationData":[OSD([sQuery(id+"F0.wireOp",EDGE,"E16.5.0.0")])]});
            var Q63;
            Q63=makeQuery(id+"F1.opExtrude","SWEPT_FACE",FACE,{"disambiguationData":[OSD([sQuery(id+"F0.wireOp",EDGE,"E16.4.0.0")])]});
            var Q64;
            Q64=makeQuery(id+"F1.opExtrude","SWEPT_FACE",FACE,{"disambiguationData":[OSD([sQuery(id+"F0.wireOp",EDGE,"E16.3.0.0")])]});
            var Q65;
            Q65=makeQuery(id+"F1.opExtrude","SWEPT_FACE",FACE,{"disambiguationData":[OSD([sQuery(id+"F0.wireOp",EDGE,"E16.2.0.0")])]});
            var Q66;
            Q66=makeQuery(id+"F1.opExtrude","SWEPT_FACE",FACE,{"disambiguationData":[OSD([sQuery(id+"F0.wireOp",EDGE,"E16.1.0.0")])]});
            var Q67;
            Q67=makeQuery(id+"F1.opExtrude","SWEPT_FACE",FACE,{"disambiguationData":[OSD([sQuery(id+"F0.wireOp",EDGE,"E15.left")])]});
            var Q68;
            Q68=makeQuery(id+"F1.opExtrude","SWEPT_FACE",FACE,{"disambiguationData":[OSD([sQuery(id+"F0.wireOp",EDGE,"E14.left")])]});
            fillet(context, id + "F6", {"entities" : qUnion([Q0, Q1, Q2, Q3, Q4, Q5, Q6, Q7, Q8, Q9, Q10, Q11, Q12, Q13, Q14, Q15, Q16, Q17, Q18, Q19, Q20, Q21, Q22, Q23, Q24, Q25, Q26, Q27, Q28, Q29, Q30, Q31, Q32, Q33, Q34, Q35, Q36, Q37, Q38, Q39, Q40, Q41, Q42, Q43, Q44, Q45, Q46, Q47, Q48, Q49, Q50, Q51, Q52, Q53, Q54, Q55, Q56, Q57, Q58, Q59, Q60, Q61, Q62, Q63, Q64, Q65, Q66, Q67, Q68]), "radius" : 0.5 * mm, "tangentPropagation" : true, "allowEdgeOverflow" : false});
        }
    });
